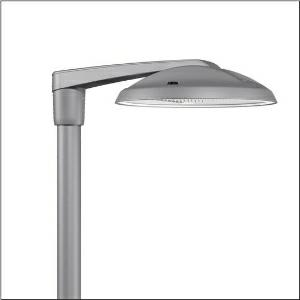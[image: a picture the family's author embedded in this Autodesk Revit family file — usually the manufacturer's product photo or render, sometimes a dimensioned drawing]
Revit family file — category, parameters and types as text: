
# Revit family: dl_50_mini___st1_0a_5xa248d33s08le_b034
name_source: partatom
category: Lighting Fixtures
units: mm (PartAtom-declared; Revit-internal decimal feet)

## family parameters
Cut with Voids When Loaded = No
Host = Face
Light Source = No
Part Type = Normal
Room Calculation Point = No
Round Connector Dimension = Use Diameter
Shared = No

## types (1)
- --- (1 x LED, 10040 lm, 66.3 W, 3000K)
    Apparent Load = 66 VA
    CIE Flux Codes = 37 72 97 100 100
    Color Rendering = 70
    Color Temperature = 3000K
    Default Elevation = 1800 mm
    Description = DL 50 mini, mast luminaire, primary light control with lens, of PMMA, primary optical cover: cover, of toughened safety glass, transparent, light distribution: ST1.0a, light emission: direct distribution, primary light characteristic: asymmetric, installation type: post-top, side-entry, LED, High Power LED, rated luminous flux: 10.040lm, luminous efficacy: 152lm/W, light colour: 730, colour temperature: 3000K, control gear: D4i, control: overheat protection, constant luminous flux control, time-dependent luminous flux control, flexible luminous flux parameterisation, mains connection: 230..240V, AC, 50/60Hz, connection cable pre-assembled, cable length: 8,5m, start of lifetime: 66W, end of service life: 68W, reduction: 32W, luminaire housing, of diecast aluminium, powder-coated, SITECO metallic grey (DB 702S), inclination adjustable: 0°, 5°, 10° (post-top) | 0°, -5°, -10°, -15° (side-entry), please order mast post-top element or mast side-entry element separately, diameter: 500mm, height: 115mm, post-top: for spigot size d x l = 76 x 100mm; with reducer (optional accessory) 60 x 100mm | side-entry: for spigot size d x l = 60 x 100mm; with reducer (optional accessory) 42 x 100mm, mounting height: 4..6m, Smart Interface above, protection rating (complete): IP66, insulation class (complete): insulation class II (safety insulation), certification: CE, ENEC, ENEC+, VDE, impact resistance: IK08, permissible operating ambient temperature for outdoor applications: -25..+40°C, standard-compliant lighting for roads and squares, packaging unit: 1 piece

Light Distribution: ST1.0a
    Height = 115 mm
    Lamp = 1 x LED
    Lamp Light Flux = 10040 lm
    Lamp Power = 66.3 W
    Lamp count = 1
    Length = 500 mm
    Luminous efficacy = 151 lm/W
    Manufacturer = Siteco
    ModVariant = No
    Model = 5XA248D33S08LE
    Number of Poles = 1
    OnlyDefault = Yes
    Power Factor = 1
    Product Name = DL 50 mini | ST1.0a
    Product group = mast luminaire | pylon top
    ProductGroupID = 6100
    Protection Class = Protection class II
    Protection Degree = IP 66
    RLX_Detail_Level = 1
    RLX_Emergency_Light_Flux = 0 lm
    RLX_Emergency_Type = 0
    RLX_Emergency_Type_DB = No
    RlxData = <blob elided: 106305 chars, md5=9518a3cf>
    Socket = socket
    Standby Power = 0 W
    System Light Flux = 10040 lm
    System Power = 66 W
    Type Comments = factory setting: luminous flux: 100 % | dim-lin: 254 | 691 mA
    Type Image = l_1251788.jpg
    URL = http://relux.com
    VarID = @adj_037685
    Voltage = 0 V
    Weight = 0.00 kg
    Width = 0 mm  [stored 0 ft]

note: [stored X ft] marks values corroborated as IEEE doubles in the binary element streams (Revit-internal decimal feet)

## geometry (parser evidence)
native form markers: Blend x4, Sweep x8
no freeform markers — native parametric forms only
